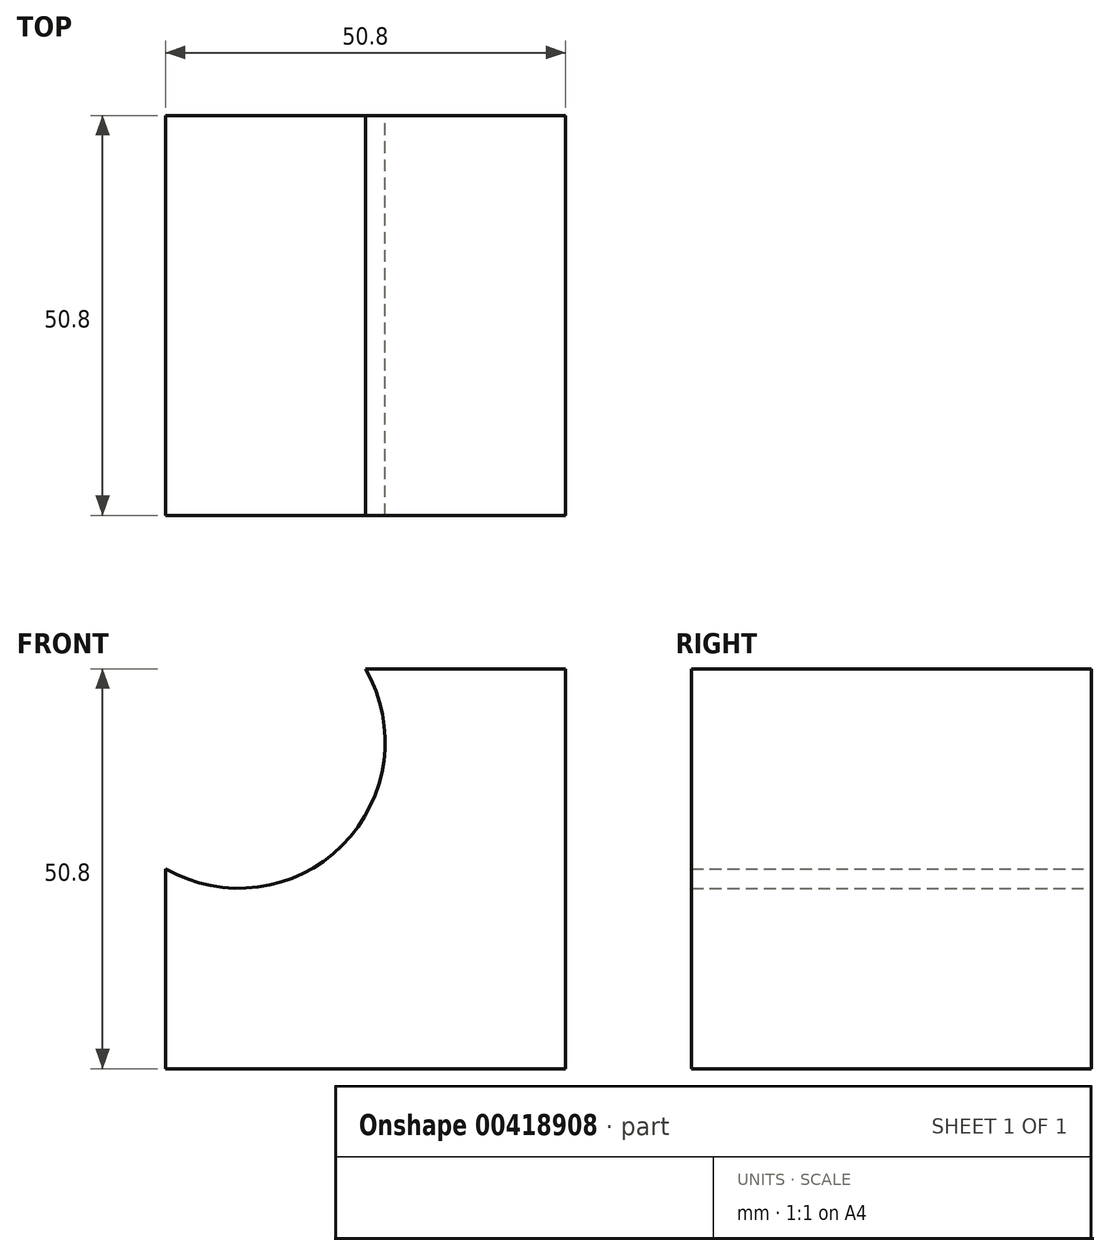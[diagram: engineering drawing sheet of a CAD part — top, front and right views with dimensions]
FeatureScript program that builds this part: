
annotation { "Feature Type Name" : "Feature", "Feature Type Description" : "" }
export const myFeature = defineFeature(function(context is Context, id is Id, definition is map)
    precondition{}
    {
        {
            var Q0;
            Q0=qCreatedBy(makeId("Front.planeOp"),FACE);
            var sketch = newSketch(context, id + "F0", { "sketchPlane" : qUnion([Q0])});
            skLineSegment(sketch, "E0", {"start": v(0, 0) * mm, "end": v(50.8, 0) * mm});
            skLineSegment(sketch, "E1", {"start": v(50.8, 0) * mm, "end": v(50.8, 50.8) * mm});
            skLineSegment(sketch, "E2", {"start": v(50.8, 50.8) * mm, "end": v(25.4, 50.8) * mm});
            skLineSegment(sketch, "E3", {"start": v(0, 0) * mm, "end": v(0, 25.4) * mm});
            skArc(sketch, "E4", {"start": v(0, 25.4) * mm, "mid": v(22.44, 28.36) * mm, "end": v(25.4, 50.8) * mm});
            skSolve(sketch);
        }
        {
            var Q0;
            Q0 = qSketchRegion(id + "F0", true);
            extrude(context, id + "F1", {"entities" : qUnion([Q0]), "depth" : 50.8 * mm});
        }
    });
